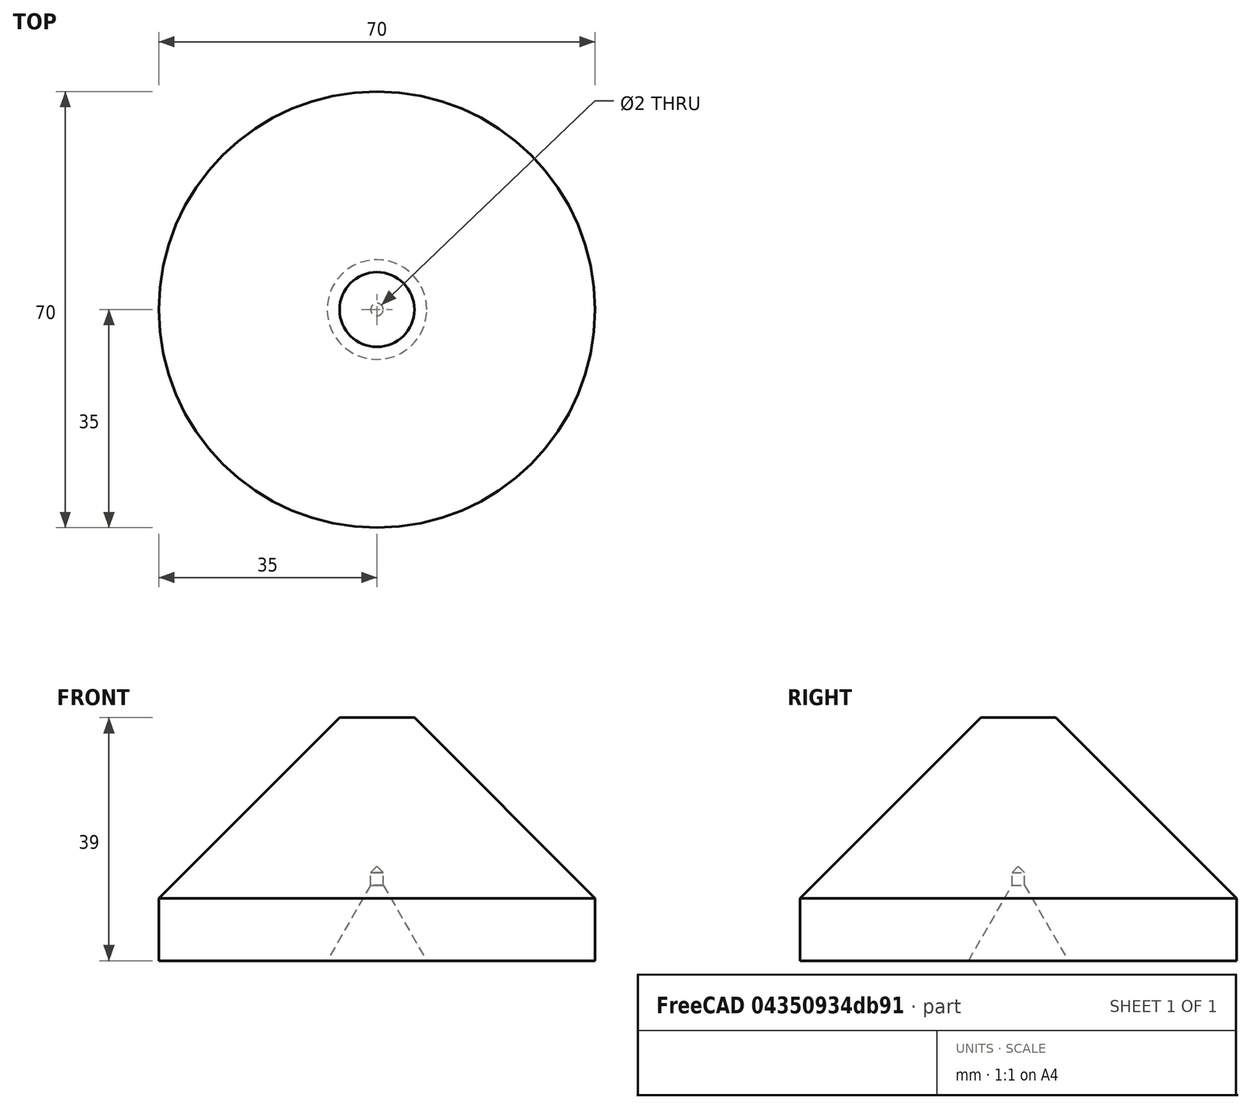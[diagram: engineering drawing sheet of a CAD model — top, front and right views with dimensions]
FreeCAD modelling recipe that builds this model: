
FCSTD DOCUMENT  (FreeCAD 0.16R)
Label: bullnose
License: All rights reserved
LicenseURL: http://en.wikipedia.org/wiki/All_rights_reserved
objects: Sketcher::SketchObject×1, PartDesign::Revolution×1
note: 3 computed .brp shape members not serialized (recipe doc carries the construction recipe); baked Part::Feature solids carry a one-line shape summary decoded from their .brp

FEATURE [Sketcher::SketchObject] Sketch
  Placement = pos=(0,0,0) rot=(0.57735,0.57735,0.57735;2.0944rad)
  sketch-geometry (8):
    g0: LineSegment StartX=0 StartY=39 StartZ=0 EndX=-6 EndY=39 EndZ=0
    g1: LineSegment StartX=-6 StartY=39 StartZ=0 EndX=-35 EndY=10 EndZ=0
    g2: LineSegment StartX=-35 StartY=10 StartZ=0 EndX=-35 EndY=0 EndZ=0
    g3: LineSegment StartX=-35 StartY=0 StartZ=0 EndX=-8 EndY=0 EndZ=0
    g4: LineSegment StartX=-8 StartY=0 StartZ=0 EndX=-1 EndY=12.1244 EndZ=0
    g5: LineSegment StartX=-1 StartY=12.1244 StartZ=0 EndX=-1 EndY=14.1244 EndZ=0
    g6: LineSegment StartX=-1 StartY=14.1244 StartZ=0 EndX=0 EndY=15.1244 EndZ=0
    g7: LineSegment StartX=0 StartY=15.1244 StartZ=0 EndX=0 EndY=39 EndZ=0
  constraints (24):
    c: PointOnObject(g0,g-2)
    c: Horizontal(g0)
    c: Coincident(g0,g1)
    c: Coincident(g1,g2)
    c: PointOnObject(g2,g-1)
    c: Coincident(g2,g3)
    c: Horizontal(g3)
    c: Coincident(g3,g4)
    c: Coincident(g4,g5)
    c: Vertical(g5)
    c: Coincident(g5,g6)
    c: PointOnObject(g6,g-2)
    c: Coincident(g6,g7)
    c: Coincident(g7,g0)
    c: Angle(g6) = 0.785398
    c: Distance(g5) = 2
    c: Angle(g4) = 1.0472
    c: Vertical(g2)
    c: Distance(g2) = 10
    c: Angle(g1) = -2.35619
    c: DistanceX(g0) = -6
    c: DistanceX(g2) = -35
    c: DistanceX(g3) = -8
    c: DistanceX(g4) = -1
FEATURE [PartDesign::Revolution] Revolution
  Angle = 360
  Axis = (0,0,1)
  Base = (0,0,0)
  Placement = pos=(0,0,0) rot=(0.57735,0.57735,0.57735;2.0944rad)
  ReferenceAxis = -> Sketch [V_Axis]
  Sketch = -> Sketch
